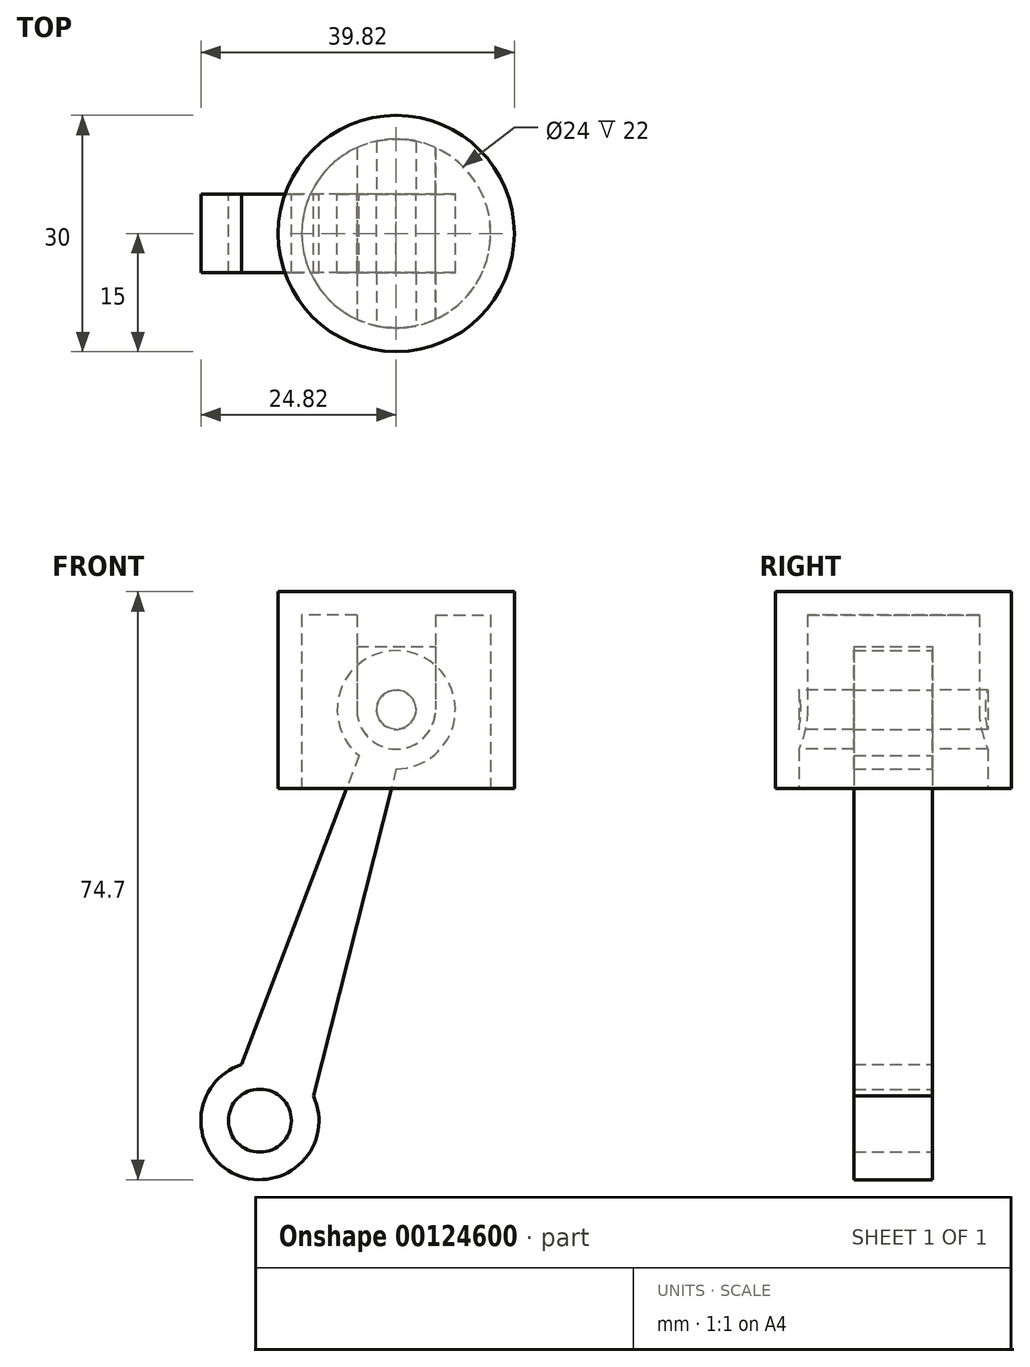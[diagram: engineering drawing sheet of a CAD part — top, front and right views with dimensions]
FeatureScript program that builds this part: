
annotation { "Feature Type Name" : "Feature", "Feature Type Description" : "" }
export const myFeature = defineFeature(function(context is Context, id is Id, definition is map)
    precondition{}
    {
        {
            var Q0;
            Q0=qCreatedBy(makeId("Front.planeOp"),FACE);
            var sketch = newSketch(context, id + "F0", { "sketchPlane" : qUnion([Q0])});
            skLineSegment(sketch, "E0", {"start": v(-38.21, 50) * mm, "end": v(61.79, 50) * mm, "construction": true});
            skLineSegment(sketch, "E1", {"start": v(-41.68, 90) * mm, "end": v(52.02, 90) * mm, "construction": true});
            skLineSegment(sketch, "E2", {"start": v(0, 0) * mm, "end": v(0, 124.4) * mm, "construction": true});
            skLineSegment(sketch, "E3", {"start": v(0, 0) * mm, "end": v(-17.32, 10) * mm});
            skLineSegment(sketch, "E4", {"start": v(-17.32, 10) * mm, "end": v(0, 62.2) * mm});
            skLineSegment(sketch, "E5", {"start": v(-60.14, 0) * mm, "end": v(58.23, 0) * mm, "construction": true});
            skLineSegment(sketch, "E6.bottom", {"start": v(-15, 77.2) * mm, "end": v(15, 77.2) * mm});
            skLineSegment(sketch, "E6.top", {"start": v(-15, 52.2) * mm, "end": v(15, 52.2) * mm});
            skLineSegment(sketch, "E6.left", {"start": v(-15, 52.2) * mm, "end": v(-15, 77.2) * mm});
            skLineSegment(sketch, "E6.right", {"start": v(15, 52.2) * mm, "end": v(15, 77.2) * mm});
            skLineSegment(sketch, "E7", {"start": v(-5, 77.2) * mm, "end": v(-5, 70.2) * mm});
            skLineSegment(sketch, "E8", {"start": v(-5, 70.2) * mm, "end": v(-5, 62.2) * mm});
            skLineSegment(sketch, "E9", {"start": v(5, 70.2) * mm, "end": v(5, 62.2) * mm});
            skArc(sketch, "E10", {"start": v(-5, 62.2) * mm, "mid": v(0, 57.2) * mm, "end": v(5, 62.2) * mm});
            skLineSegment(sketch, "E11", {"start": v(5, 70.2) * mm, "end": v(5, 77.2) * mm});
            skLineSegment(sketch, "E12", {"start": v(-5, 70.2) * mm, "end": v(5, 70.2) * mm});
            skCircle(sketch, "E13", {"center": v(0, 62.2) * mm, "radius": 2.5 * mm});
            skSolve(sketch);
        }
        {
            var Q0;
            Q0=qCreatedBy(makeId("Front.planeOp"),FACE);
            var sketch = newSketch(context, id + "F1", { "sketchPlane" : qUnion([Q0])});
            skLineSegment(sketch, "E14.0", {"start": v(0, 77.2) * mm, "end": v(15, 77.2) * mm});
            skLineSegment(sketch, "E15.0", {"start": v(15, 52.2) * mm, "end": v(15, 77.2) * mm});
            skLineSegment(sketch, "E16.0", {"start": v(0, 52.2) * mm, "end": v(15, 52.2) * mm});
            skLineSegment(sketch, "E17.0", {"start": v(0, 0) * mm, "end": v(0, 124.4) * mm});
            skPoint(sketch, "E18.orphan", {"position": v(-15, 77.2) * mm});
            skPoint(sketch, "E19.orphan", {"position": v(-15, 52.2) * mm});
            skSolve(sketch);
        }
        {
            var Q0;
            {var subQ0=sQuery(id+"F1.wireOp",EDGE,"E14.0");Q0=makeQuery(id+"F1.imprint","IMPRINT",FACE,{"disambiguationData":[TD([[makeQuery(id+"F1.imprint","IMPRINT",EDGE,{"derivedFrom":subQ0}),-1.0]])]});}
            var Q1;
            Q1=sQuery(id+"F1.wireOp",EDGE,"E17.0");
            revolve(context, id + "F2", {"entities" : qUnion([Q0]), "axis" : qUnion([Q1]), "revolveType" : RevolveType.FULL});
        }
        {
            var Q0;
            Q0=makeQuery(id+"F2.opRevolve","SWEPT_FACE",FACE,{"disambiguationData":[OSD([sQuery(id+"F1.wireOp",EDGE,"E16.0")])]});
            shell(context, id + "F3", {"entities" : qUnion([Q0]), "thickness" : 3 * mm});
        }
        {
            var Q0;
            {var subQ3=sQuery(id+"F0.wireOp",EDGE,"E8");Q0=makeQuery(id+"F0.imprint","IMPRINT",FACE,{"disambiguationData":[TD([[makeQuery(id+"F0.imprint","IMPRINT",EDGE,{"derivedFrom":subQ3}),1.0]])]});}
            extrude(context, id + "F4", {"entities" : qUnion([Q0]), "operationType" : NewBodyOperationType.ADD, "endBound" : BoundingType.UP_TO_NEXT, "oppositeDirection" : true, "depth" : 10 * mm, "hasSecondDirection" : true, "secondDirectionBound" : SecondDirectionBoundingType.UP_TO_NEXT, "secondDirectionOppositeDirection" : false, "secondDirectionDepth" : 10 * mm});
        }
        {
            var Q0;
            Q0=qCreatedBy(makeId("Front.planeOp"),FACE);
            var sketch = newSketch(context, id + "F5", { "sketchPlane" : qUnion([Q0])});
            skLineSegment(sketch, "E20", {"start": v(-5, 70.2) * mm, "end": v(-5, 62.2) * mm});
            skLineSegment(sketch, "E21", {"start": v(-5, 70.2) * mm, "end": v(5, 70.2) * mm});
            skLineSegment(sketch, "E22", {"start": v(5, 70.2) * mm, "end": v(5, 62.2) * mm});
            skArc(sketch, "E23", {"start": v(-5, 62.2) * mm, "mid": v(0, 57.2) * mm, "end": v(5, 62.2) * mm});
            skCircle(sketch, "E24", {"center": v(0, 62.2) * mm, "radius": 2.5 * mm});
            skSolve(sketch);
        }
        {
            var Q0;
            Q0=qSketchRegion(id+"F5",true);
            extrude(context, id + "F6", {"entities" : qUnion([Q0]), "operationType" : NewBodyOperationType.REMOVE, "endBound" : BoundingType.SYMMETRIC, "depth" : 10 * mm});
        }
        {
            var Q0;
            Q0=qCreatedBy(makeId("Front.planeOp"),FACE);
            var sketch = newSketch(context, id + "F7", { "sketchPlane" : qUnion([Q0])});
            skLineSegment(sketch, "E25", {"start": v(-5, 77.2) * mm, "end": v(-5, 70.2) * mm});
            skLineSegment(sketch, "E26", {"start": v(-5, 70.2) * mm, "end": v(5, 70.2) * mm});
            skLineSegment(sketch, "E27", {"start": v(5, 70.2) * mm, "end": v(5, 77.2) * mm});
            skLineSegment(sketch, "E28", {"start": v(5, 77.2) * mm, "end": v(-5, 77.2) * mm});
            skSolve(sketch);
        }
        {
            var Q0;
            Q0=qSketchRegion(id+"F7",true);
            extrude(context, id + "F8", {"entities" : qUnion([Q0]), "operationType" : NewBodyOperationType.ADD, "endBound" : BoundingType.UP_TO_NEXT, "depth" : 10.15 * mm, "hasSecondDirection" : true, "secondDirectionBound" : SecondDirectionBoundingType.UP_TO_NEXT, "secondDirectionOppositeDirection" : true, "secondDirectionDepth" : 4.75 * mm});
        }
        {
            var Q0;
            Q0=qCreatedBy(makeId("Front.planeOp"),FACE);
            var sketch = newSketch(context, id + "F9", { "sketchPlane" : qUnion([Q0])});
            skCircle(sketch, "E29", {"center": v(0, 62.2) * mm, "radius": 7.5 * mm});
            skLineSegment(sketch, "E30", {"start": v(0, 54.7) * mm, "end": v(-10.5, 13.13) * mm});
            skLineSegment(sketch, "E31", {"start": v(-10.5, 13.13) * mm, "end": v(0, 54.7) * mm});
            skLineSegment(sketch, "E32", {"start": v(-4.71, 56.37) * mm, "end": v(-19.67, 17.12) * mm});
            skCircle(sketch, "E33", {"center": v(-17.32, 10) * mm, "radius": 7.5 * mm});
            skCircle(sketch, "E34", {"center": v(-17.32, 10) * mm, "radius": 4 * mm});
            skCircle(sketch, "E35", {"center": v(0, 62.2) * mm, "radius": 2.5 * mm});
            skSolve(sketch);
        }
        {
            var Q0;
            Q0=qSketchRegion(id+"F9",true);
            extrude(context, id + "F10", {"entities" : qUnion([Q0]), "endBound" : BoundingType.SYMMETRIC, "depth" : 10 * mm});
        }
    });
